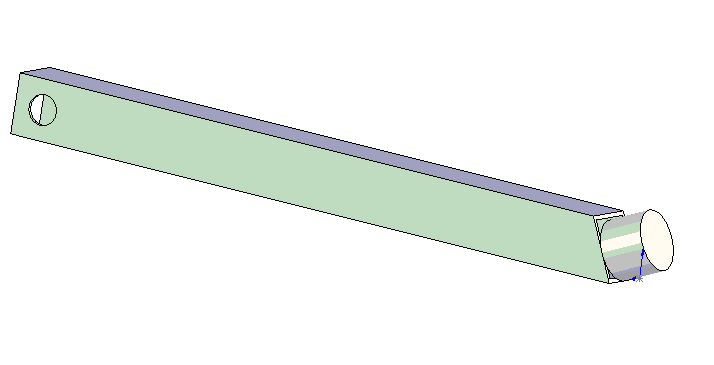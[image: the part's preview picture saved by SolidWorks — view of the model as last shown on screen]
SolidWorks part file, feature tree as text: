
SOLIDWORKS PART (.sldprt)
format: sldprt  version: not decoded by parser v0  size: 172,032 bytes
history: native  units: mm
features: sketch x4, extrude x2, cut_extrude x2 (+11 scaffold rows collapsed)
feature tree (19):
  scaffold x11  (default folders/planes/origin — collapsed)
  sketch  "Sketch1"  dims[D1=25.4mm D2=1.5875mm]
  extrude  "Extrude1"  Depth=279.4mm
  sketch  "Sketch2"  dims[D1=12.7mm D2=12.7mm D3=12.7mm]
  cut_extrude  "Cut-Extrude1"  [1 undecoded]
  sketch  "Sketch4"  dims[c1.D1=~58.979839mm c2.D1=25.0deg]
  cut_extrude  "Cut-Extrude2"  [1 undecoded]
  sketch  "Sketch5"  dims[D1=25.4mm]
  extrude  "Extrude2"  Depth=19.05mm
decode coverage: 6 of 8 modeling features carry decoded parameters
note: ~ marks probable driven/reference dimensions
note: 2 parameter values undecoded
note: suppression state not decoded; provenance and decode notes live in map.json
